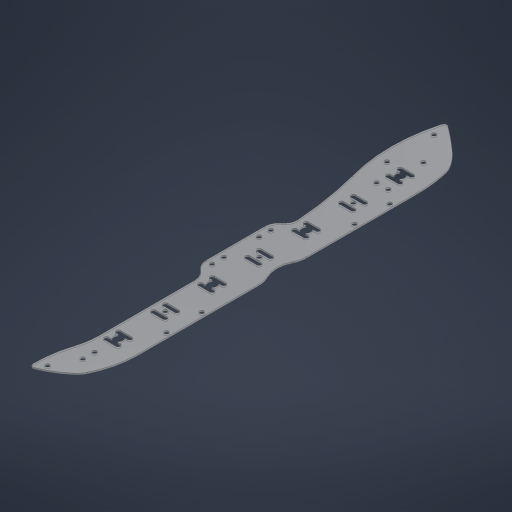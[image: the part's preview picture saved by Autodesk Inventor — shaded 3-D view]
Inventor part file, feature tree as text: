
AUTODESK INVENTOR PART (.ipt)
format: ipt  version: 2024 (Build 280153000, 153)  size: 547,840 bytes
history: native  units: in
note: dims shown in document units (in); Inventor stores cm internally (conversion verified against a paired STEP export)
features: sketch x2, extrude x2, hole x1
ambient origin geometry x8: Origin, YZ Plane, XZ Plane, XY Plane, X Axis, Y Axis, Z Axis, Center Point
bodies: Solid1 (feature_tree)
feature tree (5):
  sketch  "Sketch2"  dims[d3=0.5in d5=0.5in]
  extrude  "Extrusion1"  Depth=0.5in
  hole  "Hole3"  [1 undecoded]
  extrude  "Extrusion3"  Depth=0.1875in
  sketch  "Sketch4"  dims[d8=0.0625in d9=0.0in d37=0.25in d46=0.1875in d47=0.75in d48=0.375in d49=0.25in d50=0.5635in d51=1.0in d52=0.8108in d54=0.25in d55=1.0in d58=0.75in d77=0.375in d82=12.75in d83=1.0in d84=0.5in d85=1.5in d86=7.5in d87=2.375in d88=1.445in d89=1.0in d93=0.25in d94=0.25in d95=1.25in d96=2.875in d97=1.0in d99=1.0in d102=1.0in d103=0.5in d104=0.5in d105=3.25in d106=0.3125in d107=3.25in d108=1.5in d109=1.5in d110=3.0in d111=0.25in d112=0.75in d113=0.5in d114=0.75in d115=0.5in d116=0.25in d117=1.25in d118=0.5in d119=0.5in d121=0.75in d122=90.0deg d123=0.25in d124=0.5in d125=0.25in d126=0.0104in d127=1.0in d128=0.0in d129=4.0in d130=4.0in d131=4.0in d132=0.25in d133=0.25in d134=0.0104in d135=0.25in d136=0.25in d137=0.0104in d138=0.25in d139=0.25in d140=0.0104in d141=2.0in d143=0.25in d145=0.1875in d146=2.0in d148=0.25in d149=0.1875in d152=2.0in d153=0.25in d154=0.1875in]
note: 1 required parameter value undecoded (feature->parameter linkage not recoverable at this tier; creation-order binding heuristic only, values carry confidence <= 0.55)
